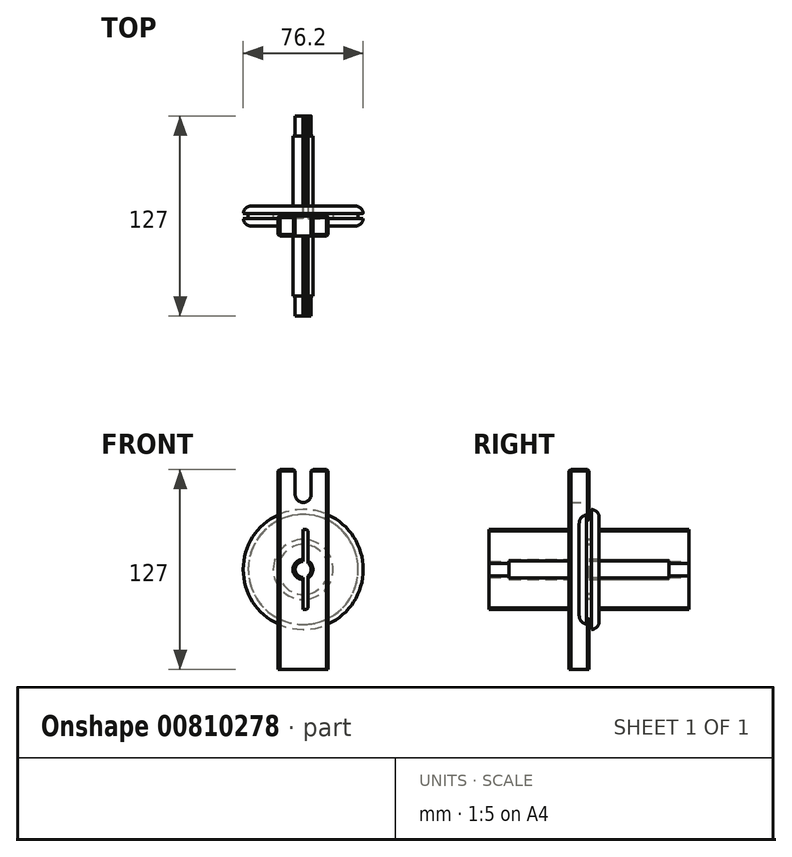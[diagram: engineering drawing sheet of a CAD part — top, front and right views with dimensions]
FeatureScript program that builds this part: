
annotation { "Feature Type Name" : "Feature", "Feature Type Description" : "" }
export const myFeature = defineFeature(function(context is Context, id is Id, definition is map)
    precondition{}
    {
        {
            var Q0;
            Q0=qCreatedBy(makeId("Front.planeOp"),FACE);
            var sketch = newSketch(context, id + "F0", { "sketchPlane" : qUnion([Q0])});
            skCircle(sketch, "E0", {"center": v(0, 0) * mm, "radius": 38.1 * mm});
            skCircle(sketch, "E1", {"center": v(0, 0) * mm, "radius": 7.62 * mm});
            skSolve(sketch);
        }
        {
            var Q0;
            Q0 = qSketchRegion(id + "F0", true);
            extrude(context, id + "F1", {"entities" : qUnion([Q0]), "endBound" : BoundingType.SYMMETRIC, "depth" : 12.7 * mm, "offsetDistance" : 25.4 * mm});
        }
        {
            var Q0;
            Q0=qCreatedBy(makeId("Front.planeOp"),FACE);
            var sketch = newSketch(context, id + "F2", { "sketchPlane" : qUnion([Q0])});
            skCircle(sketch, "E2", {"center": v(0, 0) * mm, "radius": 38.1 * mm});
            skCircle(sketch, "E3", {"center": v(0, 0) * mm, "radius": 34.93 * mm});
            skSolve(sketch);
        }
        {
            var Q0;
            Q0 = qSketchRegion(id + "F2", true);
            extrude(context, id + "F3", {"entities" : qUnion([Q0]), "operationType" : NewBodyOperationType.REMOVE, "endBound" : BoundingType.SYMMETRIC, "oppositeDirection" : true, "depth" : 3.17 * mm, "offsetDistance" : 25.4 * mm});
        }
        {
            var Q0;
            Q0=qCreatedBy(makeId("Front.planeOp"),FACE);
            var sketch = newSketch(context, id + "F4", { "sketchPlane" : qUnion([Q0])});
            skCircle(sketch, "E4", {"center": v(0, 0) * mm, "radius": 19.05 * mm});
            skCircle(sketch, "E5", {"center": v(0, 0) * mm, "radius": 6.35 * mm});
            skSolve(sketch);
        }
        {
            var Q0;
            Q0=makeQuery(id+"F4.imprint","IMPRINT",FACE,{"disambiguationData":[TD([[makeQuery(id+"F4.imprint","IMPRINT",EDGE,{"derivedFrom":sQuery(id+"F4.wireOp",EDGE,"E4")}),1.0]])]});
            extrude(context, id + "F5", {"entities" : qUnion([Q0]), "endBound" : BoundingType.SYMMETRIC, "oppositeDirection" : true, "depth" : 12.7 * mm, "offsetDistance" : 25.4 * mm});
        }
        {
            var Q0;
            Q0=qCreatedBy(makeId("Front.planeOp"),FACE);
            var sketch = newSketch(context, id + "F6", { "sketchPlane" : qUnion([Q0])});
            skLineSegment(sketch, "E6.bottom", {"start": v(15.88, -63.5) * mm, "end": v(-15.87, -63.5) * mm});
            skLineSegment(sketch, "E6.top", {"start": v(15.87, 63.5) * mm, "end": v(-15.88, 63.5) * mm});
            skLineSegment(sketch, "E6.left", {"start": v(15.88, -63.5) * mm, "end": v(15.87, 63.5) * mm});
            skLineSegment(sketch, "E6.right", {"start": v(-15.87, -63.5) * mm, "end": v(-15.88, 63.5) * mm});
            skPoint(sketch, "E6.middle", {"position": v(0, 0) * mm});
            skCircle(sketch, "E7", {"center": v(0, 47.62) * mm, "radius": 5.08 * mm});
            skLineSegment(sketch, "E8", {"start": v(-5.08, 63.5) * mm, "end": v(-5.08, 47.62) * mm});
            skLineSegment(sketch, "E9", {"start": v(5.08, 63.5) * mm, "end": v(5.08, 47.62) * mm});
            skSolve(sketch);
        }
        {
            var Q0;
            Q0=makeQuery(id+"F6.imprint","IMPRINT",FACE,{"disambiguationData":[TD([[makeQuery(id+"F6.imprint","IMPRINT",EDGE,{"derivedFrom":sQuery(id+"F6.wireOp",EDGE,"E6.bottom")}),-1.0]])]});
            extrude(context, id + "F7", {"entities" : qUnion([Q0]), "depth" : 12.7 * mm, "offsetDistance" : 25.4 * mm});
        }
        {
            var Q0;
            Q0=qCreatedBy(makeId("Front.planeOp"),FACE);
            var sketch = newSketch(context, id + "F8", { "sketchPlane" : qUnion([Q0])});
            skCircle(sketch, "E10", {"center": v(0, 0) * mm, "radius": 19.05 * mm});
            skCircle(sketch, "E11", {"center": v(0, 0) * mm, "radius": 15.88 * mm});
            skSolve(sketch);
        }
        {
            var Q0;
            Q0 = qSketchRegion(id + "F8", true);
            extrude(context, id + "F9", {"entities" : qUnion([Q0]), "operationType" : NewBodyOperationType.REMOVE, "endBound" : BoundingType.SYMMETRIC, "oppositeDirection" : true, "depth" : 3.17 * mm, "offsetDistance" : 25.4 * mm});
        }
        {
            var Q0;
            Q0=qCreatedBy(makeId("Right.planeOp"),FACE);
            var sketch = newSketch(context, id + "F10", { "sketchPlane" : qUnion([Q0])});
            skLineSegment(sketch, "E12.bottom", {"start": v(63.5, -25.4) * mm, "end": v(-63.5, -25.4) * mm});
            skLineSegment(sketch, "E12.top", {"start": v(63.5, 25.4) * mm, "end": v(-63.5, 25.4) * mm});
            skLineSegment(sketch, "E12.left", {"start": v(63.5, -25.4) * mm, "end": v(63.5, 25.4) * mm});
            skLineSegment(sketch, "E12.right", {"start": v(-63.5, -25.4) * mm, "end": v(-63.5, 25.4) * mm});
            skPoint(sketch, "E12.middle", {"position": v(0, 0) * mm});
            skSolve(sketch);
        }
        {
            var Q0;
            Q0=makeQuery(id+"F10.imprint","IMPRINT",FACE,{"disambiguationData":[TD([[makeQuery(id+"F10.imprint","IMPRINT",EDGE,{"derivedFrom":sQuery(id+"F10.wireOp",EDGE,"E12.bottom")}),-1.0]])]});
            extrude(context, id + "F11", {"entities" : qUnion([Q0]), "depth" : 3.17 * mm, "offsetDistance" : 25 * mm});
        }
        {
            var Q0;
            Q0=qCreatedBy(makeId("Front.planeOp"),FACE);
            var sketch = newSketch(context, id + "F12", { "sketchPlane" : qUnion([Q0])});
            skCircle(sketch, "E13", {"center": v(-0.2, 0) * mm, "radius": 6.35 * mm});
            skSolve(sketch);
        }
        {
            var Q0;
            Q0 = qSketchRegion(id + "F12", true);
            extrude(context, id + "F13", {"entities" : qUnion([Q0]), "endBound" : BoundingType.SYMMETRIC, "depth" : 101.6 * mm, "offsetDistance" : 25.4 * mm});
        }
        {
            var Q0;
            Q0=qCreatedBy(makeId("Front.planeOp"),FACE);
            var sketch = newSketch(context, id + "F14", { "sketchPlane" : qUnion([Q0])});
            skCircle(sketch, "E14", {"center": v(0, 0) * mm, "radius": 5.08 * mm});
            skSolve(sketch);
        }
        {
            var Q0;
            Q0 = qSketchRegion(id + "F14", true);
            extrude(context, id + "F15", {"entities" : qUnion([Q0]), "operationType" : NewBodyOperationType.ADD, "endBound" : BoundingType.SYMMETRIC, "depth" : 127 * mm, "offsetDistance" : 25 * mm});
        }
        {
            var Q0;
            Q0=makeQuery(id+"F7.opExtrude","CAP_EDGE",EDGE,{"disambiguationData":[OSD([sQuery(id+"F6.wireOp",EDGE,"E6.left")])],"isStart":true});
            var Q1;
            Q1=makeQuery(id+"F7.opExtrude","SWEPT_EDGE",EDGE,{"disambiguationData":[OSD([sQuery(id+"F6.wireOp",EDGE,"E6.top"),sQuery(id+"F6.wireOp",EDGE,"E6.right")])]});
            var Q2;
            Q2=makeQuery(id+"F7.opExtrude","CAP_EDGE",EDGE,{"disambiguationData":[OSD([sQuery(id+"F6.wireOp",EDGE,"E6.top")])],"isStart":false});
            var Q3;
            Q3=makeQuery(id+"F7.opExtrude","CAP_EDGE",EDGE,{"disambiguationData":[OSD([sQuery(id+"F6.wireOp",EDGE,"E6.top")])],"isStart":true});
            var Q4;
            Q4=makeQuery(id+"F7.opExtrude","SWEPT_EDGE",EDGE,{"disambiguationData":[OSD([sQuery(id+"F6.wireOp",EDGE,"E6.top"),sQuery(id+"F6.wireOp",EDGE,"E6.left")])]});
            var Q5;
            Q5=makeQuery(id+"F7.opExtrude","CAP_EDGE",EDGE,{"disambiguationData":[OSD([sQuery(id+"F6.wireOp",EDGE,"E6.left")])],"isStart":false});
            var Q6;
            Q6=makeQuery(id+"F7.opExtrude","CAP_EDGE",EDGE,{"disambiguationData":[OSD([sQuery(id+"F6.wireOp",EDGE,"E6.right")])],"isStart":true});
            var Q7;
            Q7=makeQuery(id+"F7.opExtrude","CAP_EDGE",EDGE,{"disambiguationData":[OSD([sQuery(id+"F6.wireOp",EDGE,"E6.right")])],"isStart":false});
            var Q8;
            Q8=makeQuery(id+"F7.opExtrude","SWEPT_EDGE",EDGE,{"disambiguationData":[OSD([sQuery(id+"F6.wireOp",EDGE,"E6.top"),sQuery(id+"F6.wireOp",EDGE,"E8")])]});
            var Q9;
            Q9=makeQuery(id+"F7.opExtrude","SWEPT_EDGE",EDGE,{"disambiguationData":[OSD([sQuery(id+"F6.wireOp",EDGE,"E6.top"),sQuery(id+"F6.wireOp",EDGE,"E9")])]});
            chamfer(context, id + "F16", {"entities" : qUnion([Q0, Q1, Q2, Q3, Q4, Q5, Q6, Q7, Q8, Q9]), "width" : 1 * mm, "tangentPropagation" : true});
        }
        {
            var Q0;
            Q0=makeQuery(id+"F11.opExtrude","CAP_EDGE",EDGE,{"disambiguationData":[OSD([sQuery(id+"F10.wireOp",EDGE,"E12.top")])],"isStart":false});
            var Q1;
            Q1=makeQuery(id+"F11.opExtrude","CAP_EDGE",EDGE,{"disambiguationData":[OSD([sQuery(id+"F10.wireOp",EDGE,"E12.bottom")])],"isStart":false});
            chamfer(context, id + "F17", {"entities" : qUnion([Q0, Q1]), "width" : 1 * mm, "tangentPropagation" : true});
        }
        {
            var Q0;
            Q0=makeQuery(id+"F1.opExtrude","CAP_EDGE",EDGE,{"disambiguationData":[OSD([sQuery(id+"F0.wireOp",EDGE,"E0")])],"isStart":true});
            var Q1;
            Q1=makeQuery(id+"F1.opExtrude","CAP_EDGE",EDGE,{"disambiguationData":[OSD([sQuery(id+"F0.wireOp",EDGE,"E0")])],"isStart":false});
            var Q2;
            Q2=makeQuery(id+"F5.opExtrude","CAP_EDGE",EDGE,{"disambiguationData":[OSD([sQuery(id+"F4.wireOp",EDGE,"E4")])],"isStart":true});
            var Q3;
            Q3=makeQuery(id+"F5.opExtrude","CAP_EDGE",EDGE,{"disambiguationData":[OSD([sQuery(id+"F4.wireOp",EDGE,"E4")])],"isStart":false});
            fillet(context, id + "F18", {"entities" : qUnion([Q0, Q1, Q2, Q3]), "radius" : 5.08 * mm, "tangentPropagation" : true, "allowEdgeOverflow" : false});
        }
        {
            var Q0;
            Q0=makeQuery(id+"F5.opExtrude","CAP_FACE",FACE,{"disambiguationData":[OSD([sQuery(id+"F4.wireOp",EDGE,"E4"),sQuery(id+"F4.wireOp",EDGE,"E5")])],"isStart":true});
            var sketch = newSketch(context, id + "F19", { "sketchPlane" : qUnion([Q0])});
            skCircle(sketch, "E15", {"center": v(-1.06, 12.35) * mm, "radius": 1.59 * mm});
            skSolve(sketch);
        }
        {
            var Q0;
            Q0=makeQuery(id+"F19.imprint","IMPRINT",FACE,{"disambiguationData":[TD([[makeQuery(id+"F19.imprint","IMPRINT",EDGE,{"derivedFrom":sQuery(id+"F19.wireOp",EDGE,"E15")}),1.0]])]});
            var Q1;
            Q1=sQuery(id+"F19.wireOp",EDGE,"E15");
            extrude(context, id + "F20", {"entities" : qUnion([Q0]), "operationType" : NewBodyOperationType.ADD, "surfaceOperationType" : NewSurfaceOperationType.ADD, "surfaceEntities" : qUnion([Q1]), "depth" : 2 * mm, "offsetDistance" : 25.4 * mm});
        }
        {
            var Q0;
            Q0=makeQuery(id+"F1.opExtrude","CAP_FACE",FACE,{"disambiguationData":[OSD([sQuery(id+"F0.wireOp",EDGE,"E0"),sQuery(id+"F0.wireOp",EDGE,"E1")])],"isStart":false});
            var sketch = newSketch(context, id + "F21", { "sketchPlane" : qUnion([Q0])});
            skCircle(sketch, "E16", {"center": v(-5.34, 30.99) * mm, "radius": 1.59 * mm});
            skSolve(sketch);
        }
        {
            var Q0;
            Q0 = qSketchRegion(id + "F21", true);
            extrude(context, id + "F22", {"entities" : qUnion([Q0]), "operationType" : NewBodyOperationType.ADD, "depth" : 2 * mm, "offsetDistance" : 25.4 * mm});
        }
    });
